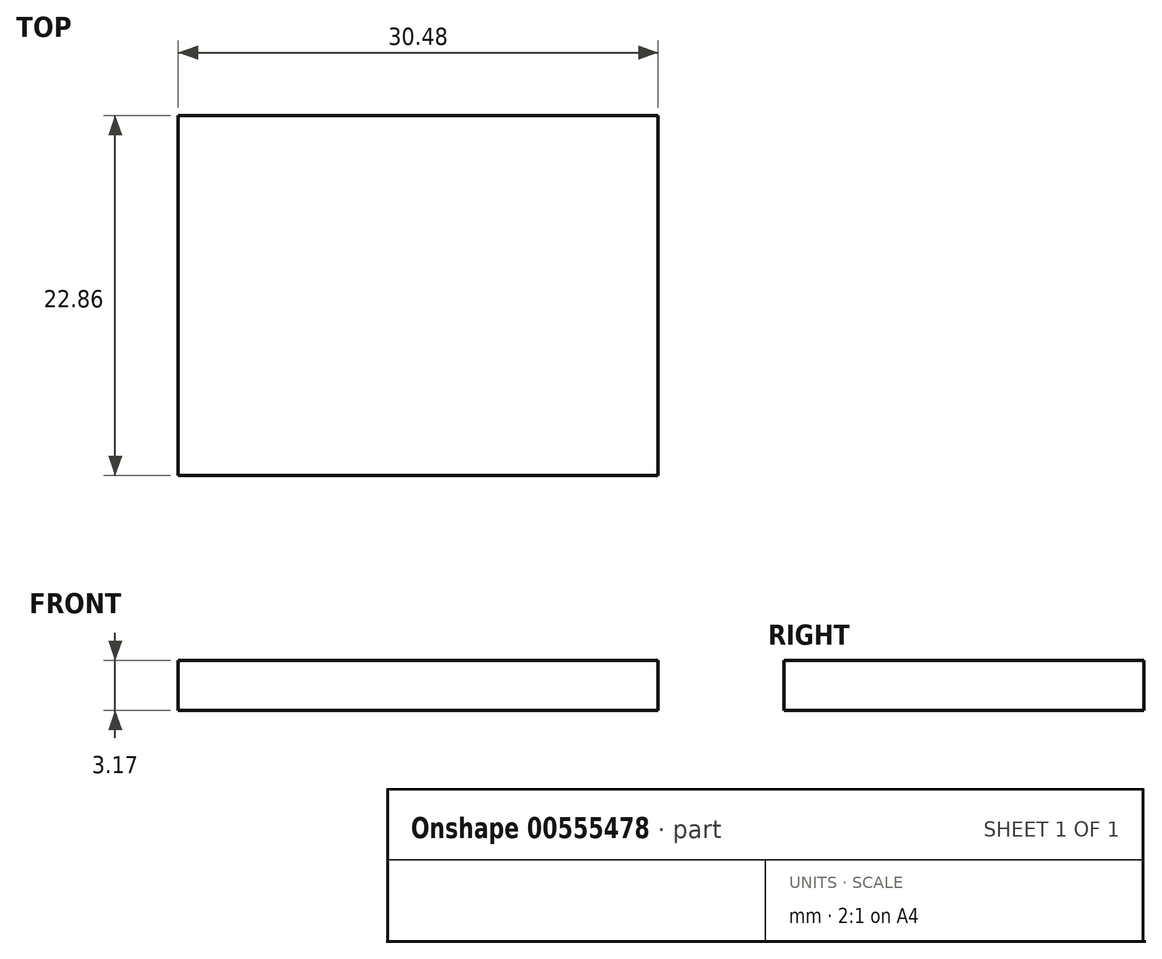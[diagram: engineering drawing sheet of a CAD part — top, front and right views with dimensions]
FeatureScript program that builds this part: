
annotation { "Feature Type Name" : "Feature", "Feature Type Description" : "" }
export const myFeature = defineFeature(function(context is Context, id is Id, definition is map)
    precondition{}
    {
        {
            var Q0;
            Q0=qCreatedBy(makeId("Top.planeOp"),FACE);
            var sketch = newSketch(context, id + "F0", { "sketchPlane" : qUnion([Q0])});
            skLineSegment(sketch, "E0.bottom", {"start": v(-15.24, 11.43) * mm, "end": v(15.24, 11.43) * mm});
            skLineSegment(sketch, "E0.top", {"start": v(-15.24, -11.43) * mm, "end": v(15.24, -11.43) * mm});
            skLineSegment(sketch, "E0.left", {"start": v(-15.24, 11.43) * mm, "end": v(-15.24, -11.43) * mm});
            skLineSegment(sketch, "E0.right", {"start": v(15.24, 11.43) * mm, "end": v(15.24, -11.43) * mm});
            skPoint(sketch, "E0.middle", {"position": v(0, 0) * mm});
            skSolve(sketch);
        }
        {
            var Q0;
            Q0=makeQuery(id+"F0.imprint","IMPRINT",FACE,{"disambiguationData":[TD([[makeQuery(id+"F0.imprint","IMPRINT",EDGE,{"derivedFrom":sQuery(id+"F0.wireOp",EDGE,"E0.bottom")}),-1.0]])]});
            extrude(context, id + "F1", {"entities" : qUnion([Q0]), "depth" : 3.17 * mm, "offsetDistance" : 25.4 * mm});
        }
    });
